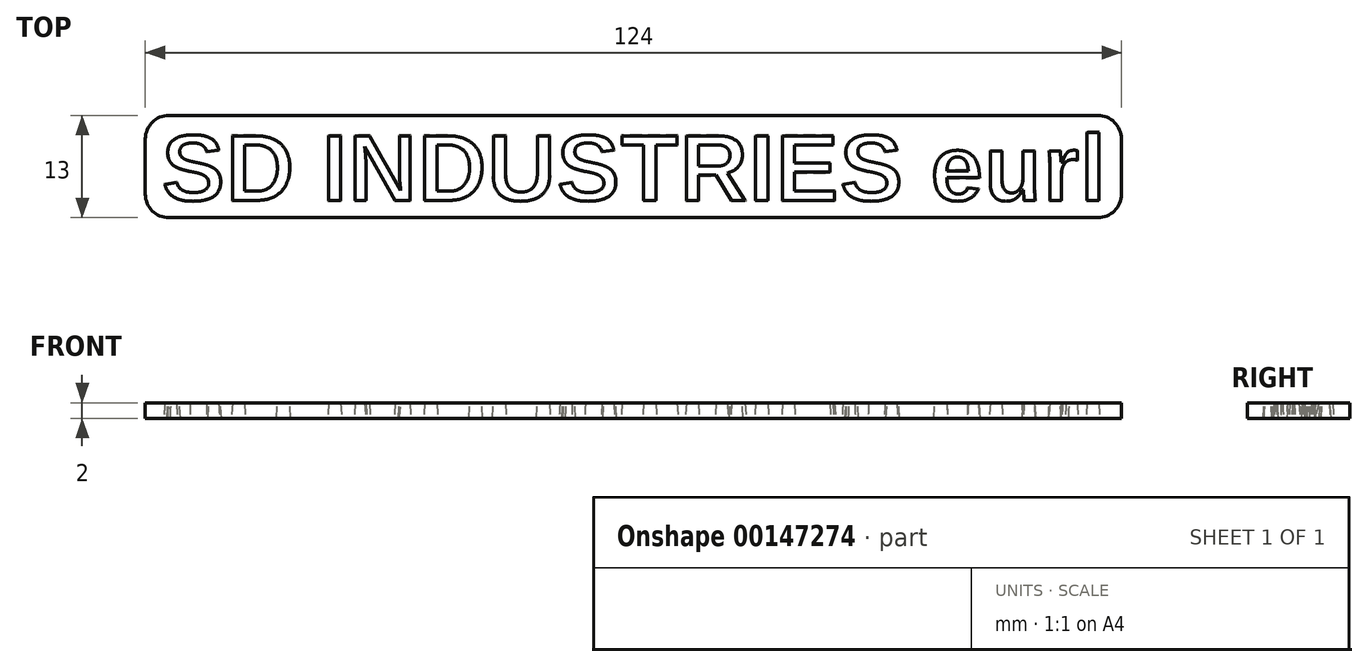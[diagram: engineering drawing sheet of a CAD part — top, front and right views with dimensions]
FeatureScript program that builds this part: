
annotation { "Feature Type Name" : "Feature", "Feature Type Description" : "" }
export const myFeature = defineFeature(function(context is Context, id is Id, definition is map)
    precondition{}
    {
        {
            var Q0;
            Q0=qCreatedBy(makeId("Top.planeOp"),FACE);
            var sketch = newSketch(context, id + "F0", { "sketchPlane" : qUnion([Q0])});
            skText(sketch, "E0", { "text": "SD INDUSTRIES eurl", "fontName": "Arimo-Bold.ttf"});
            skLineSegment(sketch, "E1.bottom", {"start": v(59, -2.1) * mm, "end": v(-59, -2.1) * mm});
            skLineSegment(sketch, "E1.top", {"start": v(59, 10.9) * mm, "end": v(-59, 10.9) * mm});
            skLineSegment(sketch, "E1.left", {"start": v(62, 0.9) * mm, "end": v(62, 7.9) * mm});
            skLineSegment(sketch, "E1.right", {"start": v(-62, 0.9) * mm, "end": v(-62, 7.9) * mm});
            skPoint(sketch, "E1.middle", {"position": v(0, 4.4) * mm});
            skPoint(sketch, "E2.visualSharp", {"position": v(-62, 10.9) * mm});
            skArc(sketch, "E2.filletArc", {"start": v(-59, 10.9) * mm, "mid": v(-61.12, 10.01) * mm, "end": v(-62, 7.9) * mm});
            skPoint(sketch, "E3.visualSharp", {"position": v(-62, -2.1) * mm});
            skArc(sketch, "E3.filletArc", {"start": v(-62, 0.9) * mm, "mid": v(-61.12, -1.23) * mm, "end": v(-59, -2.1) * mm});
            skPoint(sketch, "E4.visualSharp", {"position": v(62, -2.1) * mm});
            skArc(sketch, "E4.filletArc", {"start": v(59, -2.1) * mm, "mid": v(61.12, -1.23) * mm, "end": v(62, 0.9) * mm});
            skPoint(sketch, "E5.visualSharp", {"position": v(62, 10.9) * mm});
            skArc(sketch, "E5.filletArc", {"start": v(62, 7.9) * mm, "mid": v(61.12, 10.01) * mm, "end": v(59, 10.9) * mm});
            skArc(sketch, "E6.0", {"start": v(64, 7.9) * mm, "mid": v(62.54, 11.43) * mm, "end": v(59, 12.9) * mm});
            skLineSegment(sketch, "E6.1", {"start": v(64, 0.9) * mm, "end": v(64, 7.9) * mm});
            skLineSegment(sketch, "E6.2", {"start": v(59, 12.9) * mm, "end": v(-59, 12.9) * mm});
            skArc(sketch, "E6.3", {"start": v(59, -4.1) * mm, "mid": v(62.54, -2.64) * mm, "end": v(64, 0.9) * mm});
            skArc(sketch, "E6.4", {"start": v(-59, 12.9) * mm, "mid": v(-62.54, 11.43) * mm, "end": v(-64, 7.9) * mm});
            skLineSegment(sketch, "E6.5", {"start": v(-64, 0.9) * mm, "end": v(-64, 7.9) * mm});
            skArc(sketch, "E6.6", {"start": v(-64, 0.9) * mm, "mid": v(-62.54, -2.64) * mm, "end": v(-59, -4.1) * mm});
            skLineSegment(sketch, "E6.7", {"start": v(59, -4.1) * mm, "end": v(-59, -4.1) * mm});
            const initialGuessF0  = {"E0": [-0.06, 0, 1, 0, 0.00879]};
            skSetInitialGuess(sketch, initialGuessF0);
            skSolve(sketch);
        }
        {
            var Q0;
            Q0=qCreatedBy(makeId("Top.planeOp"),FACE);
            var sketch = newSketch(context, id + "F1", { "sketchPlane" : qUnion([Q0])});
            skLineSegment(sketch, "E7.0", {"start": v(59, 12.9) * mm, "end": v(-59, 12.9) * mm});
            skArc(sketch, "E8.0", {"start": v(-59, 12.9) * mm, "mid": v(-62.54, 11.43) * mm, "end": v(-64, 7.9) * mm});
            skLineSegment(sketch, "E9.0", {"start": v(-64, 0.9) * mm, "end": v(-64, 7.9) * mm});
            skArc(sketch, "E10.0", {"start": v(-64, 0.9) * mm, "mid": v(-62.54, -2.64) * mm, "end": v(-59, -4.1) * mm});
            skLineSegment(sketch, "E11.0", {"start": v(59, -4.1) * mm, "end": v(-59, -4.1) * mm});
            skArc(sketch, "E12.0", {"start": v(59, -4.1) * mm, "mid": v(62.54, -2.64) * mm, "end": v(64, 0.9) * mm});
            skLineSegment(sketch, "E13.0", {"start": v(64, 0.9) * mm, "end": v(64, 7.9) * mm});
            skArc(sketch, "E14.0", {"start": v(64, 7.9) * mm, "mid": v(62.54, 11.43) * mm, "end": v(59, 12.9) * mm});
            skSolve(sketch);
        }
        {
            var Q0;
            Q0=makeQuery(id+"F0.imprint","IMPRINT",FACE,{"disambiguationData":[TD([[makeQuery(id+"F0.imprint","IMPRINT",EDGE,{"derivedFrom":sQuery(id+"F0.wireOp",EDGE,"E0.sketch_text.stroke-0")}),1.0]])]});
            var Q1;
            Q1=makeQuery(id+"F0.imprint","IMPRINT",FACE,{"disambiguationData":[TD([[makeQuery(id+"F0.imprint","IMPRINT",EDGE,{"derivedFrom":sQuery(id+"F0.wireOp",EDGE,"E0.sketch_text.stroke-39")}),1.0]])]});
            var Q2;
            Q2=makeQuery(id+"F0.imprint","IMPRINT",FACE,{"disambiguationData":[TD([[makeQuery(id+"F0.imprint","IMPRINT",EDGE,{"derivedFrom":sQuery(id+"F0.wireOp",EDGE,"E0.sketch_text.stroke-70")}),1.0]])]});
            var Q3;
            Q3=makeQuery(id+"F0.imprint","IMPRINT",FACE,{"disambiguationData":[TD([[makeQuery(id+"F0.imprint","IMPRINT",EDGE,{"derivedFrom":sQuery(id+"F0.wireOp",EDGE,"E0.sketch_text.stroke-142")}),1.0]])]});
            var Q4;
            Q4=makeQuery(id+"F0.imprint","IMPRINT",FACE,{"disambiguationData":[TD([[makeQuery(id+"F0.imprint","IMPRINT",EDGE,{"derivedFrom":sQuery(id+"F0.wireOp",EDGE,"E0.sketch_text.stroke-208")}),1.0]])]});
            extrude(context, id + "F2", {"entities" : qUnion([Q0, Q1, Q2, Q3, Q4]), "depth" : 2 * mm, "hasDraft" : true, "draftAngle" : 3 * degree});
        }
        {
            var Q0;
            Q0=makeQuery(id+"F2.opExtrude","CAP_EDGE",EDGE,{"disambiguationData":[OSD([sQuery(id+"F0.wireOp",EDGE,"E1.top"),sQuery(id+"F1.wireOp",EDGE,"E7.0"),sQuery(id+"F1.wireOp",EDGE,"E8.0"),sQuery(id+"F1.wireOp",EDGE,"E9.0"),sQuery(id+"F1.wireOp",EDGE,"E10.0"),sQuery(id+"F1.wireOp",EDGE,"E11.0"),sQuery(id+"F1.wireOp",EDGE,"E12.0"),sQuery(id+"F1.wireOp",EDGE,"E13.0"),sQuery(id+"F1.wireOp",EDGE,"E14.0")])],"isStart":false});
            var Q1;
            Q1=makeQuery(id+"F2.opExtrude","CAP_EDGE",EDGE,{"disambiguationData":[OSD([sQuery(id+"F0.wireOp",EDGE,"E2.filletArc"),sQuery(id+"F1.wireOp",EDGE,"E7.0"),sQuery(id+"F1.wireOp",EDGE,"E8.0"),sQuery(id+"F1.wireOp",EDGE,"E9.0"),sQuery(id+"F1.wireOp",EDGE,"E10.0"),sQuery(id+"F1.wireOp",EDGE,"E11.0"),sQuery(id+"F1.wireOp",EDGE,"E12.0"),sQuery(id+"F1.wireOp",EDGE,"E13.0"),sQuery(id+"F1.wireOp",EDGE,"E14.0")])],"isStart":false});
            var Q2;
            Q2=makeQuery(id+"F2.opExtrude","CAP_EDGE",EDGE,{"disambiguationData":[OSD([sQuery(id+"F0.wireOp",EDGE,"E1.right"),sQuery(id+"F1.wireOp",EDGE,"E7.0"),sQuery(id+"F1.wireOp",EDGE,"E8.0"),sQuery(id+"F1.wireOp",EDGE,"E9.0"),sQuery(id+"F1.wireOp",EDGE,"E10.0"),sQuery(id+"F1.wireOp",EDGE,"E11.0"),sQuery(id+"F1.wireOp",EDGE,"E12.0"),sQuery(id+"F1.wireOp",EDGE,"E13.0"),sQuery(id+"F1.wireOp",EDGE,"E14.0")])],"isStart":false});
            var Q3;
            Q3=makeQuery(id+"F2.opExtrude","CAP_EDGE",EDGE,{"disambiguationData":[OSD([sQuery(id+"F0.wireOp",EDGE,"E3.filletArc"),sQuery(id+"F1.wireOp",EDGE,"E7.0"),sQuery(id+"F1.wireOp",EDGE,"E8.0"),sQuery(id+"F1.wireOp",EDGE,"E9.0"),sQuery(id+"F1.wireOp",EDGE,"E10.0"),sQuery(id+"F1.wireOp",EDGE,"E11.0"),sQuery(id+"F1.wireOp",EDGE,"E12.0"),sQuery(id+"F1.wireOp",EDGE,"E13.0"),sQuery(id+"F1.wireOp",EDGE,"E14.0")])],"isStart":false});
            var Q4;
            Q4=makeQuery(id+"F2.opExtrude","CAP_EDGE",EDGE,{"disambiguationData":[OSD([sQuery(id+"F0.wireOp",EDGE,"E1.bottom"),sQuery(id+"F1.wireOp",EDGE,"E7.0"),sQuery(id+"F1.wireOp",EDGE,"E8.0"),sQuery(id+"F1.wireOp",EDGE,"E9.0"),sQuery(id+"F1.wireOp",EDGE,"E10.0"),sQuery(id+"F1.wireOp",EDGE,"E11.0"),sQuery(id+"F1.wireOp",EDGE,"E12.0"),sQuery(id+"F1.wireOp",EDGE,"E13.0"),sQuery(id+"F1.wireOp",EDGE,"E14.0")])],"isStart":false});
            var Q5;
            Q5=makeQuery(id+"F2.opExtrude","CAP_EDGE",EDGE,{"disambiguationData":[OSD([sQuery(id+"F0.wireOp",EDGE,"E5.filletArc"),sQuery(id+"F1.wireOp",EDGE,"E7.0"),sQuery(id+"F1.wireOp",EDGE,"E8.0"),sQuery(id+"F1.wireOp",EDGE,"E9.0"),sQuery(id+"F1.wireOp",EDGE,"E10.0"),sQuery(id+"F1.wireOp",EDGE,"E11.0"),sQuery(id+"F1.wireOp",EDGE,"E12.0"),sQuery(id+"F1.wireOp",EDGE,"E13.0"),sQuery(id+"F1.wireOp",EDGE,"E14.0")])],"isStart":false});
            var Q6;
            Q6=makeQuery(id+"F2.opExtrude","CAP_EDGE",EDGE,{"disambiguationData":[OSD([sQuery(id+"F0.wireOp",EDGE,"E1.left"),sQuery(id+"F1.wireOp",EDGE,"E7.0"),sQuery(id+"F1.wireOp",EDGE,"E8.0"),sQuery(id+"F1.wireOp",EDGE,"E9.0"),sQuery(id+"F1.wireOp",EDGE,"E10.0"),sQuery(id+"F1.wireOp",EDGE,"E11.0"),sQuery(id+"F1.wireOp",EDGE,"E12.0"),sQuery(id+"F1.wireOp",EDGE,"E13.0"),sQuery(id+"F1.wireOp",EDGE,"E14.0")])],"isStart":false});
            var Q7;
            Q7=makeQuery(id+"F2.opExtrude","CAP_EDGE",EDGE,{"disambiguationData":[OSD([sQuery(id+"F0.wireOp",EDGE,"E4.filletArc"),sQuery(id+"F1.wireOp",EDGE,"E7.0"),sQuery(id+"F1.wireOp",EDGE,"E8.0"),sQuery(id+"F1.wireOp",EDGE,"E9.0"),sQuery(id+"F1.wireOp",EDGE,"E10.0"),sQuery(id+"F1.wireOp",EDGE,"E11.0"),sQuery(id+"F1.wireOp",EDGE,"E12.0"),sQuery(id+"F1.wireOp",EDGE,"E13.0"),sQuery(id+"F1.wireOp",EDGE,"E14.0")])],"isStart":false});
            chamfer(context, id + "F3", {"entities" : qUnion([Q0, Q1, Q2, Q3, Q4, Q5, Q6, Q7]), "chamferType" : ChamferType.OFFSET_ANGLE, "width" : 2 * mm, "oppositeDirection" : true, "angle" : 3 * degree, "tangentPropagation" : true});
        }
    });
